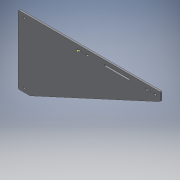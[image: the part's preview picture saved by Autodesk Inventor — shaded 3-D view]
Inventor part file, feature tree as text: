
AUTODESK INVENTOR PART (.ipt)
format: ipt  version: 2019 (Build 230136000, 136)  size: 191,488 bytes
history: native  units: in
note: dims shown in document units (in); Inventor stores cm internally (conversion verified against a paired STEP export)
features: reference x37, sketch x5, extrude x4, other x4, fillet x1, projected_geometry x1, helix x1
ambient origin geometry x8: Origin, YZ Plane, XZ Plane, XY Plane, X Axis, Y Axis, Z Axis, Center Point
bodies: Solid1 (feature_tree)
feature tree (53):
  extrude  "Extrusion1"  Depth=0.1575in TaperAngle=0.0deg
  fillet  "Fillet1"  Radius=0.0787in
  sketch  "Sketch2"  dims[d5=0.0079in d6=0.0079in]
  extrude  "Extrusion2"  Depth=0.0079in
  extrude  "Extrusion3"  Depth=0.0079in
  extrude  "Extrusion4"  Depth=0.1575in
  sketch  "Sketch1"  dims[d0=0.3937in d2=0.1575in d3=0.0in d4=0.0787in]
  reference  "Reference1"
  reference  "Reference2"
  reference  "Reference3"
  reference  "Reference4"
  sketch  "Sketch3"  dims[d7=0.0079in d8=0.0079in]
  reference  "Reference5"
  reference  "Reference6"
  reference  "Reference7"
  reference  "Reference8"
  reference  "Reference9"
  reference  "Reference10"
  reference  "Reference11"
  reference  "Reference12"
  reference  "Reference13"
  reference  "Reference14"
  projected_geometry  "Projected Loop1"
  reference  "Reference15"
  reference  "Reference16"
  reference  "Reference17"
  reference  "Reference18"
  reference  "Reference19"
  reference  "Reference20"
  reference  "Reference21"
  reference  "Reference22"
  reference  "Reference23"
  reference  "Reference24"
  reference  "Reference25"
  reference  "Reference26"
  reference  "Reference27"
  reference  "Reference28"
  reference  "Reference29"
  reference  "Reference30"
  reference  "Reference31"
  reference  "Reference32"
  reference  "Reference33"
  reference  "Reference34"
  sketch  "Sketch4"  dims[d9=0.126in d10=0.126in d11=0.1575in d12=0.0in]
  reference  "Reference35"
  sketch  "Sketch5"  dims[d13=0.3937in d14=0.3937in d15=0.1969in d16=0.1969in d17=0.1575in d18=0.0in d19=0.0079in d20=1.0in d21=0.0in]
  reference  "Reference36"
  reference  "Reference37"
  other  "<userpath>\Documents\CAD Files\Helix DLP\Helix DLP.iam"
  helix  "Helix DLP.iam"  [1 undecoded]
  other  "ProjectorMount 1:1"
  other  "30X30 - T-slot - Aluminium Profile_CPY_CPY:1"
  other  "Projector:1"
note: 1 required parameter value undecoded (feature->parameter linkage not recoverable at this tier; creation-order binding heuristic only, values carry confidence <= 0.55)
